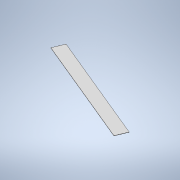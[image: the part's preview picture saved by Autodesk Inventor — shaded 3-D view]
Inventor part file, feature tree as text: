
AUTODESK INVENTOR PART (.ipt)
format: ipt  version: 2022 (Build 260153000, 153)  size: 97,792 bytes
history: native  units: mm
features: extrude x1, sketch x1
ambient origin geometry x8: Origin, YZ Plane, XZ Plane, XY Plane, X Axis, Y Axis, Z Axis, Center Point
bodies: Solid1 (feature_tree)
feature tree (2):
  extrude  "Extrusion1"  TaperAngle=22.5deg  [1 undecoded]
  sketch  "Sketch1"  dims[d2=1000.0mm d3=22.5deg d4=100.0mm d5=2.0mm d6=0.0mm]
note: 1 required parameter value undecoded (feature->parameter linkage not recoverable at this tier; creation-order binding heuristic only, values carry confidence <= 0.55)
